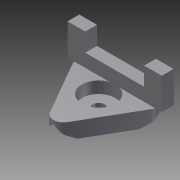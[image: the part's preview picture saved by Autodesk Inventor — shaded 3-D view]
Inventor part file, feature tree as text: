
AUTODESK INVENTOR PART (.ipt)
format: ipt  version: 2011 (Build 150239000, 239)  size: 180,736 bytes
history: native  units: in
note: dims shown in document units (in); Inventor stores cm internally (conversion verified against a paired STEP export)
features: sketch x5, extrude x4, other x1, imported_body x1, hole x1
ambient origin geometry x8: Origin, YZ Plane, XZ Plane, XY Plane, X Axis, Y Axis, Z Axis, Center Point
feature tree (12):
  other  "TricornerGround"
  imported_body  "Base1"
  extrude  "Extrusion1"  Depth=0.1181in
  hole  "Hole1"  [1 undecoded]
  extrude  "Extrusion2"  Depth=0.4724in
  extrude  "Extrusion3"  Depth=0.1181in
  extrude  "Extrusion4"  Depth=0.2953in
  sketch  "Sketch2"  dims[d0=0.1575in d1=0.0in d2=0.1181in]
  sketch  "Sketch3"  dims[d3=0.1181in d4=0.2362in d5=0.1575in d6=0.0787in d7=90.0deg d8=0.315in d9=0.8108in d10=0.3346in]
  sketch  "Sketch4"  dims[d11=0.1181in d12=0.0in d13=0.4724in]
  sketch  "Sketch5"  dims[d14=0.9449in d15=0.1181in]
  sketch  "Sketch6"  dims[d16=0.315in d17=0.0in d18=0.2953in d19=0.5906in d20=0.1839in d21=0.0in]
note: 1 required parameter value undecoded (feature->parameter linkage not recoverable at this tier; creation-order binding heuristic only, values carry confidence <= 0.55)
